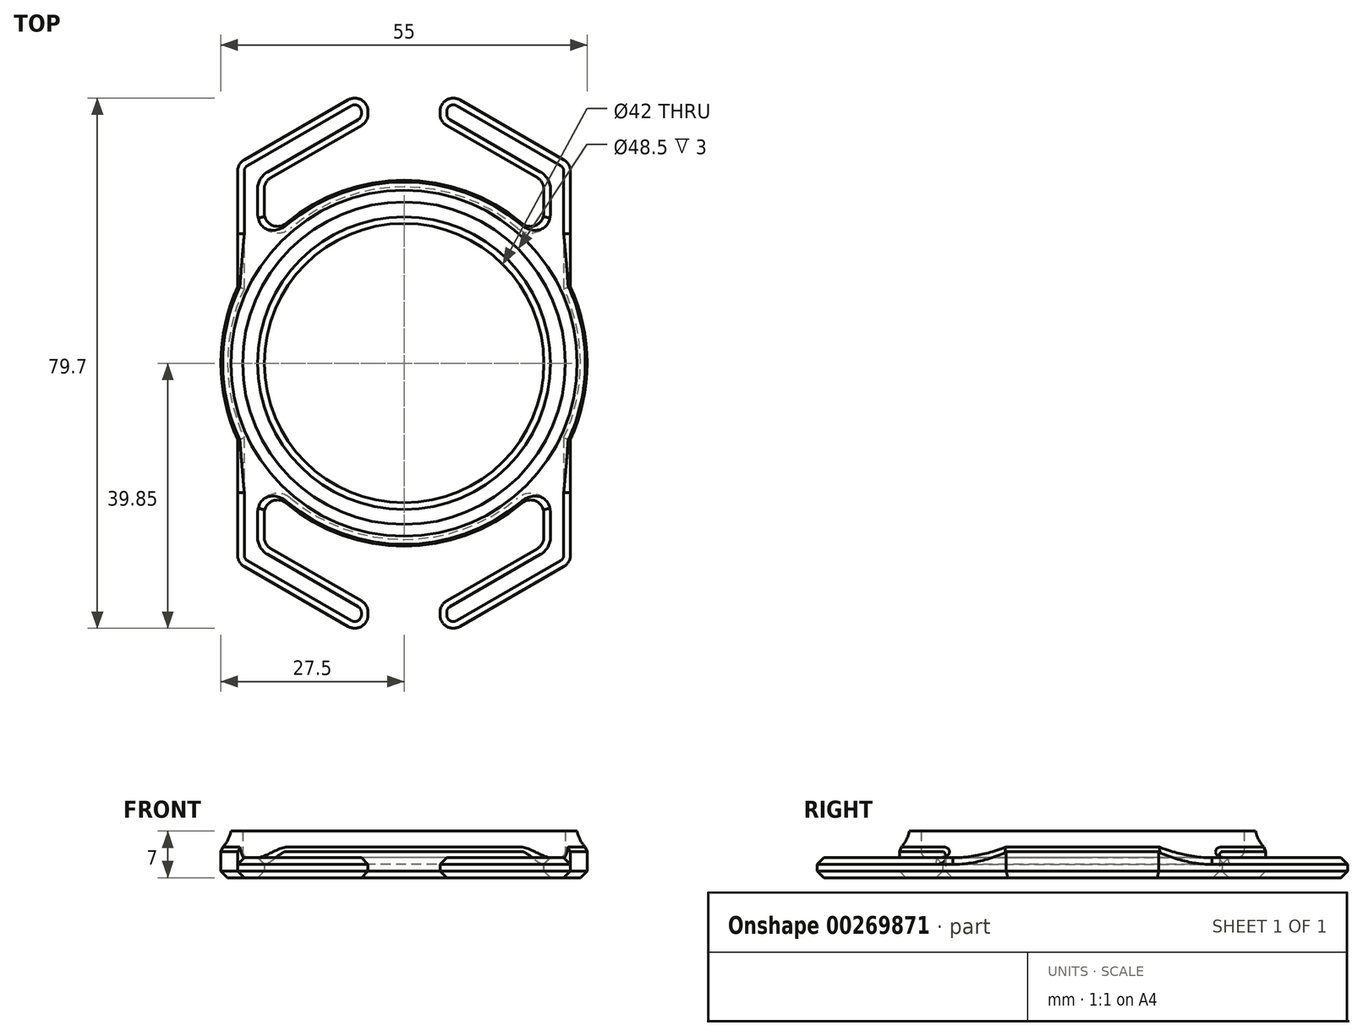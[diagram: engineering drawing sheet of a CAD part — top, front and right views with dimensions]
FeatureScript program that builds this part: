
annotation { "Feature Type Name" : "Feature", "Feature Type Description" : "" }
export const myFeature = defineFeature(function(context is Context, id is Id, definition is map)
    precondition{}
    {
        {
            var Q0;
            Q0=qCreatedBy(makeId("Top.planeOp"),FACE);
            var sketch = newSketch(context, id + "F0", { "sketchPlane" : qUnion([Q0])});
            skCircle(sketch, "E0", {"center": v(0, 0) * mm, "radius": 25 * mm});
            skLineSegment(sketch, "E1", {"start": v(-21, 27.3) * mm, "end": v(-5.41, 36.3) * mm});
            skLineSegment(sketch, "E2", {"start": v(-5.41, 36.3) * mm, "end": v(-5.41, 41.3) * mm});
            skLineSegment(sketch, "E3", {"start": v(-5.41, 41.3) * mm, "end": v(-25, 30) * mm});
            skLineSegment(sketch, "E4", {"start": v(-25, 30) * mm, "end": v(-25, 0) * mm});
            skLineSegment(sketch, "E5", {"start": v(-21, 27.3) * mm, "end": v(-21, 0) * mm});
            skCircle(sketch, "E6", {"center": v(0, 0) * mm, "radius": 21 * mm});
            skLineSegment(sketch, "E7", {"start": v(0, 0) * mm, "end": v(-21, 0) * mm, "construction": true});
            skLineSegment(sketch, "E8", {"start": v(-25, 0) * mm, "end": v(-21, 0) * mm});
            skLineSegment(sketch, "E9", {"start": v(0, 0) * mm, "end": v(0, 21) * mm, "construction": true});
            skLineSegment(sketch, "E10.MirrorCS", {"start": v(21, 27.3) * mm, "end": v(21, 0) * mm});
            skLineSegment(sketch, "E11.MirrorCS", {"start": v(25, 30) * mm, "end": v(25, 0) * mm});
            skLineSegment(sketch, "E12.MirrorCS", {"start": v(5.41, 41.3) * mm, "end": v(25, 30) * mm});
            skLineSegment(sketch, "E13.MirrorCS", {"start": v(21, 27.3) * mm, "end": v(5.41, 36.3) * mm});
            skLineSegment(sketch, "E14.MirrorCS", {"start": v(5.41, 36.3) * mm, "end": v(5.41, 41.3) * mm});
            skLineSegment(sketch, "E15.MirrorCS", {"start": v(-21, -27.3) * mm, "end": v(-21, 0) * mm});
            skLineSegment(sketch, "E16.MirrorCS", {"start": v(-25, -30) * mm, "end": v(-25, 0) * mm});
            skLineSegment(sketch, "E17.MirrorCS", {"start": v(-5.41, -41.3) * mm, "end": v(-25, -30) * mm});
            skLineSegment(sketch, "E18.MirrorCS", {"start": v(-21, -27.3) * mm, "end": v(-5.41, -36.3) * mm});
            skLineSegment(sketch, "E19.MirrorCS", {"start": v(-5.41, -36.3) * mm, "end": v(-5.41, -41.3) * mm});
            skLineSegment(sketch, "E20.MirrorCS", {"start": v(21, -27.3) * mm, "end": v(21, 0) * mm});
            skLineSegment(sketch, "E21.MirrorCS", {"start": v(25, -30) * mm, "end": v(25, 0) * mm});
            skLineSegment(sketch, "E22.MirrorCS", {"start": v(5.41, -41.3) * mm, "end": v(25, -30) * mm});
            skLineSegment(sketch, "E23.MirrorCS", {"start": v(21, -27.3) * mm, "end": v(5.41, -36.3) * mm});
            skLineSegment(sketch, "E24.MirrorCS", {"start": v(5.41, -36.3) * mm, "end": v(5.41, -41.3) * mm});
            skSolve(sketch);
        }
        {
            var Q0;
            Q0 = qSketchRegion(id + "F0", true);
            extrude(context, id + "F1", {"entities" : qUnion([Q0]), "depth" : 3 * mm});
        }
        {
            var Q0;
            Q0=makeQuery(id+"F1.opExtrude","CAP_FACE",FACE,{"disambiguationData":[OSD([sQuery(id+"F0.wireOp",EDGE,"E0"),sQuery(id+"F0.wireOp",EDGE,"E6")])],"isStart":false});
            var sketch = newSketch(context, id + "F2", { "sketchPlane" : qUnion([Q0])});
            skCircle(sketch, "E25", {"center": v(0, 0) * mm, "radius": 26 * mm});
            skCircle(sketch, "E26", {"center": v(0, 0) * mm, "radius": 24.25 * mm});
            skSolve(sketch);
        }
        {
            var Q0;
            Q0 = qSketchRegion(id + "F2", true);
            extrude(context, id + "F3", {"entities" : qUnion([Q0]), "operationType" : NewBodyOperationType.ADD, "depth" : 4 * mm});
        }
        {
            var Q0;
            Q0=qCreatedBy(makeId("Top.planeOp"),FACE);
            var sketch = newSketch(context, id + "F4", { "sketchPlane" : qUnion([Q0])});
            skCircle(sketch, "E27", {"center": v(0, 0) * mm, "radius": 27.5 * mm});
            skCircle(sketch, "E28", {"center": v(0, 0) * mm, "radius": 23 * mm});
            skSolve(sketch);
        }
        {
            var Q0;
            Q0 = qSketchRegion(id + "F4", true);
            extrude(context, id + "F5", {"entities" : qUnion([Q0]), "operationType" : NewBodyOperationType.ADD, "depth" : 3 * mm});
        }
        {
            var Q0;
            Q0=makeQuery(id+"F5.boolean.opBoolean","INTERSECT",EDGE,{"derivedFrom":[makeQuery(id+"F1.opExtrude","SWEPT_FACE",FACE,{"disambiguationData":[OSD([sQuery(id+"F0.wireOp",EDGE,"E5")])]}),makeQuery(id+"F5.opExtrude","SWEPT_FACE",FACE,{"disambiguationData":[OSD([sQuery(id+"F4.wireOp",EDGE,"E27")])]})]});
            var Q1;
            Q1=makeQuery(id+"F1.opExtrude","SWEPT_EDGE",EDGE,{"disambiguationData":[OSD([sQuery(id+"F0.wireOp",EDGE,"E1"),sQuery(id+"F0.wireOp",EDGE,"E5")])]});
            var Q2;
            Q2=makeQuery(id+"F1.opExtrude","SWEPT_EDGE",EDGE,{"disambiguationData":[OSD([sQuery(id+"F0.wireOp",EDGE,"E1"),sQuery(id+"F0.wireOp",EDGE,"E2")])]});
            var Q3;
            Q3=makeQuery(id+"F1.opExtrude","SWEPT_EDGE",EDGE,{"disambiguationData":[OSD([sQuery(id+"F0.wireOp",EDGE,"E2"),sQuery(id+"F0.wireOp",EDGE,"E3")])]});
            var Q4;
            Q4=makeQuery(id+"F1.opExtrude","SWEPT_EDGE",EDGE,{"disambiguationData":[OSD([sQuery(id+"F0.wireOp",EDGE,"E13.MirrorCS"),sQuery(id+"F0.wireOp",EDGE,"E14.MirrorCS")])]});
            var Q5;
            Q5=makeQuery(id+"F1.opExtrude","SWEPT_EDGE",EDGE,{"disambiguationData":[OSD([sQuery(id+"F0.wireOp",EDGE,"E12.MirrorCS"),sQuery(id+"F0.wireOp",EDGE,"E14.MirrorCS")])]});
            var Q6;
            Q6=makeQuery(id+"F1.opExtrude","SWEPT_EDGE",EDGE,{"disambiguationData":[OSD([sQuery(id+"F0.wireOp",EDGE,"E10.MirrorCS"),sQuery(id+"F0.wireOp",EDGE,"E13.MirrorCS")])]});
            var Q7;
            Q7=makeQuery(id+"F5.boolean.opBoolean","INTERSECT",EDGE,{"derivedFrom":[makeQuery(id+"F1.opExtrude","SWEPT_FACE",FACE,{"disambiguationData":[OSD([sQuery(id+"F0.wireOp",EDGE,"E10.MirrorCS")])]}),makeQuery(id+"F5.opExtrude","SWEPT_FACE",FACE,{"disambiguationData":[OSD([sQuery(id+"F4.wireOp",EDGE,"E27")])]})]});
            var Q8;
            Q8=makeQuery(id+"F1.opExtrude","SWEPT_EDGE",EDGE,{"disambiguationData":[OSD([sQuery(id+"F0.wireOp",EDGE,"E11.MirrorCS"),sQuery(id+"F0.wireOp",EDGE,"E12.MirrorCS")])]});
            var Q9;
            Q9=makeQuery(id+"F1.opExtrude","SWEPT_EDGE",EDGE,{"disambiguationData":[OSD([sQuery(id+"F0.wireOp",EDGE,"E3"),sQuery(id+"F0.wireOp",EDGE,"E4")])]});
            var Q10;
            Q10=makeQuery(id+"F5.boolean.opBoolean","INTERSECT",EDGE,{"derivedFrom":[makeQuery(id+"F1.opExtrude","SWEPT_FACE",FACE,{"disambiguationData":[OSD([sQuery(id+"F0.wireOp",EDGE,"E15.MirrorCS")])]}),makeQuery(id+"F5.opExtrude","SWEPT_FACE",FACE,{"disambiguationData":[OSD([sQuery(id+"F4.wireOp",EDGE,"E27")])]})]});
            var Q11;
            Q11=makeQuery(id+"F5.boolean.opBoolean","INTERSECT",EDGE,{"derivedFrom":[makeQuery(id+"F1.opExtrude","SWEPT_FACE",FACE,{"disambiguationData":[OSD([sQuery(id+"F0.wireOp",EDGE,"E20.MirrorCS")])]}),makeQuery(id+"F5.opExtrude","SWEPT_FACE",FACE,{"disambiguationData":[OSD([sQuery(id+"F4.wireOp",EDGE,"E27")])]})]});
            var Q12;
            Q12=makeQuery(id+"F1.opExtrude","SWEPT_EDGE",EDGE,{"disambiguationData":[OSD([sQuery(id+"F0.wireOp",EDGE,"E20.MirrorCS"),sQuery(id+"F0.wireOp",EDGE,"E23.MirrorCS")])]});
            var Q13;
            Q13=makeQuery(id+"F1.opExtrude","SWEPT_EDGE",EDGE,{"disambiguationData":[OSD([sQuery(id+"F0.wireOp",EDGE,"E23.MirrorCS"),sQuery(id+"F0.wireOp",EDGE,"E24.MirrorCS")])]});
            var Q14;
            Q14=makeQuery(id+"F1.opExtrude","SWEPT_EDGE",EDGE,{"disambiguationData":[OSD([sQuery(id+"F0.wireOp",EDGE,"E22.MirrorCS"),sQuery(id+"F0.wireOp",EDGE,"E24.MirrorCS")])]});
            var Q15;
            Q15=makeQuery(id+"F1.opExtrude","SWEPT_EDGE",EDGE,{"disambiguationData":[OSD([sQuery(id+"F0.wireOp",EDGE,"E15.MirrorCS"),sQuery(id+"F0.wireOp",EDGE,"E18.MirrorCS")])]});
            var Q16;
            Q16=makeQuery(id+"F1.opExtrude","SWEPT_EDGE",EDGE,{"disambiguationData":[OSD([sQuery(id+"F0.wireOp",EDGE,"E18.MirrorCS"),sQuery(id+"F0.wireOp",EDGE,"E19.MirrorCS")])]});
            var Q17;
            Q17=makeQuery(id+"F1.opExtrude","SWEPT_EDGE",EDGE,{"disambiguationData":[OSD([sQuery(id+"F0.wireOp",EDGE,"E17.MirrorCS"),sQuery(id+"F0.wireOp",EDGE,"E19.MirrorCS")])]});
            var Q18;
            Q18=makeQuery(id+"F1.opExtrude","SWEPT_EDGE",EDGE,{"disambiguationData":[OSD([sQuery(id+"F0.wireOp",EDGE,"E21.MirrorCS"),sQuery(id+"F0.wireOp",EDGE,"E22.MirrorCS")])]});
            var Q19;
            Q19=makeQuery(id+"F1.opExtrude","SWEPT_EDGE",EDGE,{"disambiguationData":[OSD([sQuery(id+"F0.wireOp",EDGE,"E16.MirrorCS"),sQuery(id+"F0.wireOp",EDGE,"E17.MirrorCS")])]});
            fillet(context, id + "F6", {"entities" : qUnion([Q0, Q1, Q2, Q3, Q4, Q5, Q6, Q7, Q8, Q9, Q10, Q11, Q12, Q13, Q14, Q15, Q16, Q17, Q18, Q19]), "radius" : 2 * mm, "tangentPropagation" : true, "allowEdgeOverflow" : false});
        }
        {
            var Q0;
            Q0=makeQuery(id+"F3.opExtrude","CAP_EDGE",EDGE,{"disambiguationData":[OSD([sQuery(id+"F2.wireOp",EDGE,"E26")])],"isStart":true});
            fillet(context, id + "F7", {"entities" : qUnion([Q0]), "radius" : 1 * mm, "tangentPropagation" : true, "allowEdgeOverflow" : false});
        }
        {
            var Q0;
            {var subQ0=sQuery(id+"F0.wireOp",EDGE,"E21.MirrorCS");var subQ1=sQuery(id+"F0.wireOp",EDGE,"E20.MirrorCS");var subQ2=sQuery(id+"F0.wireOp",EDGE,"E16.MirrorCS");var subQ3=sQuery(id+"F0.wireOp",EDGE,"E15.MirrorCS");var subQ4=sQuery(id+"F0.wireOp",EDGE,"E11.MirrorCS");var subQ5=sQuery(id+"F0.wireOp",EDGE,"E10.MirrorCS");var subQ6=sQuery(id+"F0.wireOp",EDGE,"E5");var subQ7=sQuery(id+"F0.wireOp",EDGE,"E4");var subQ8=makeQuery(id+"F1.opExtrude","CAP_FACE",FACE,{"disambiguationData":[OSD([sQuery(id+"F0.wireOp",EDGE,"E0"),sQuery(id+"F0.wireOp",EDGE,"E1"),sQuery(id+"F0.wireOp",EDGE,"E2"),sQuery(id+"F0.wireOp",EDGE,"E3"),subQ7,subQ6,sQuery(id+"F0.wireOp",EDGE,"E6"),subQ5,subQ4,sQuery(id+"F0.wireOp",EDGE,"E12.MirrorCS"),sQuery(id+"F0.wireOp",EDGE,"E13.MirrorCS"),sQuery(id+"F0.wireOp",EDGE,"E14.MirrorCS"),subQ3,subQ2,sQuery(id+"F0.wireOp",EDGE,"E17.MirrorCS"),sQuery(id+"F0.wireOp",EDGE,"E18.MirrorCS"),sQuery(id+"F0.wireOp",EDGE,"E19.MirrorCS"),subQ1,subQ0,sQuery(id+"F0.wireOp",EDGE,"E22.MirrorCS"),sQuery(id+"F0.wireOp",EDGE,"E23.MirrorCS"),sQuery(id+"F0.wireOp",EDGE,"E24.MirrorCS")])],"isStart":false});var subQ9=makeQuery(id+"F1.opExtrude","SWEPT_FACE",FACE,{"disambiguationData":[OSD([subQ4,subQ0])]});var subQ10=sQuery(id+"F2.wireOp",EDGE,"E25");var subQ11=makeQuery(id+"F3.opExtrude","SWEPT_FACE",FACE,{"disambiguationData":[OSD([subQ10])]});var subQ12=makeQuery(id+"F3.opExtrude","CAP_FACE",FACE,{"disambiguationData":[OSD([subQ10,sQuery(id+"F2.wireOp",EDGE,"E26")])],"isStart":true});var subQ13=makeQuery(id+"F3.opExtrude","CAP_EDGE",EDGE,{"disambiguationData":[OSD([subQ10])],"isStart":true});var subQ14=makeQuery(id+"F1.opExtrude","SWEPT_FACE",FACE,{"disambiguationData":[OSD([subQ7,subQ2])]});var subQ15=makeQuery(id+"F1.opExtrude","SWEPT_FACE",FACE,{"disambiguationData":[OSD([subQ1])]});var subQ16=makeQuery(id+"F1.opExtrude","SWEPT_FACE",FACE,{"disambiguationData":[OSD([subQ3])]});var subQ17=makeQuery(id+"F1.opExtrude","SWEPT_FACE",FACE,{"disambiguationData":[OSD([subQ5])]});var subQ18=makeQuery(id+"F1.opExtrude","SWEPT_FACE",FACE,{"disambiguationData":[OSD([subQ6])]});Q0=makeQuery(id+"F5.boolean.opBoolean","MERGE",EDGE,{"derivedFrom":[makeQuery(id+"F3.boolean.opBoolean","SPLIT",EDGE,{"disambiguationData":[topologyDisambiguationEdgeConnected([subQ11,subQ12]),TD([subQ18])],"derivedFrom":subQ13}),makeQuery(id+"F3.boolean.opBoolean","SPLIT",EDGE,{"disambiguationData":[topologyDisambiguationEdgeConnected([subQ11,subQ12]),TD([subQ16])],"derivedFrom":subQ13}),makeQuery(id+"F3.boolean.opBoolean","SPLIT",EDGE,{"disambiguationData":[topologyDisambiguationEdgeConnected([subQ8,subQ11]),TD([subQ18])],"derivedFrom":subQ13}),makeQuery(id+"F3.boolean.opBoolean","SPLIT",EDGE,{"disambiguationData":[topologyDisambiguationEdgeConnected([subQ8,subQ11]),TD([subQ17])],"derivedFrom":subQ13}),makeQuery(id+"F3.boolean.opBoolean","SPLIT",EDGE,{"disambiguationData":[topologyDisambiguationEdgeConnected([subQ8,subQ11]),TD([subQ16])],"derivedFrom":subQ13}),makeQuery(id+"F3.boolean.opBoolean","SPLIT",EDGE,{"disambiguationData":[topologyDisambiguationEdgeConnected([subQ8,subQ11]),TD([subQ15])],"derivedFrom":subQ13}),makeQuery(id+"F3.boolean.opBoolean","SPLIT",EDGE,{"disambiguationData":[topologyDisambiguationEdgeConnected([subQ11,subQ12]),TD([subQ14])],"derivedFrom":subQ13}),makeQuery(id+"F3.boolean.opBoolean","SPLIT",EDGE,{"disambiguationData":[topologyDisambiguationEdgeConnected([subQ11,subQ12]),TD([subQ9])],"derivedFrom":subQ13})]});}
            fillet(context, id + "F8", {"entities" : qUnion([Q0]), "radius" : 5 * mm, "tangentPropagation" : true, "allowEdgeOverflow" : false});
        }
        {
            var Q0;
            {var subQ0=sQuery(id+"F4.wireOp",EDGE,"E27");var subQ2=sQuery(id+"F0.wireOp",EDGE,"E15.MirrorCS");Q0=makeQuery(id+"F5.boolean.opBoolean","SPLIT",EDGE,{"disambiguationData":[TD([makeQuery(id+"F1.opExtrude","SWEPT_FACE",FACE,{"disambiguationData":[OSD([subQ2])]})])],"derivedFrom":makeQuery(id+"F5.opExtrude","CAP_EDGE",EDGE,{"disambiguationData":[OSD([subQ0])],"isStart":true})});}
            var Q1;
            {var subQ0=sQuery(id+"F0.wireOp",EDGE,"E20.MirrorCS");var subQ1=makeQuery(id+"F1.opExtrude","SWEPT_FACE",FACE,{"disambiguationData":[OSD([subQ0])]});var subQ3=sQuery(id+"F4.wireOp",EDGE,"E27");var subQ4=sQuery(id+"F0.wireOp",EDGE,"E15.MirrorCS");var subQ5=makeQuery(id+"F1.opExtrude","SWEPT_FACE",FACE,{"disambiguationData":[OSD([subQ4])]});var subQ6=sQuery(id+"F0.wireOp",EDGE,"E24.MirrorCS");var subQ7=sQuery(id+"F0.wireOp",EDGE,"E23.MirrorCS");var subQ8=sQuery(id+"F0.wireOp",EDGE,"E22.MirrorCS");var subQ9=sQuery(id+"F0.wireOp",EDGE,"E21.MirrorCS");var subQ10=sQuery(id+"F0.wireOp",EDGE,"E19.MirrorCS");var subQ11=sQuery(id+"F0.wireOp",EDGE,"E18.MirrorCS");var subQ12=sQuery(id+"F0.wireOp",EDGE,"E17.MirrorCS");var subQ13=sQuery(id+"F0.wireOp",EDGE,"E16.MirrorCS");var subQ14=sQuery(id+"F0.wireOp",EDGE,"E14.MirrorCS");var subQ15=sQuery(id+"F0.wireOp",EDGE,"E13.MirrorCS");var subQ16=sQuery(id+"F0.wireOp",EDGE,"E12.MirrorCS");var subQ17=sQuery(id+"F0.wireOp",EDGE,"E11.MirrorCS");var subQ18=sQuery(id+"F0.wireOp",EDGE,"E10.MirrorCS");var subQ19=sQuery(id+"F0.wireOp",EDGE,"E6");var subQ20=sQuery(id+"F0.wireOp",EDGE,"E5");var subQ21=sQuery(id+"F0.wireOp",EDGE,"E4");var subQ22=sQuery(id+"F0.wireOp",EDGE,"E3");var subQ23=sQuery(id+"F0.wireOp",EDGE,"E2");var subQ24=sQuery(id+"F0.wireOp",EDGE,"E1");var subQ25=sQuery(id+"F0.wireOp",EDGE,"E0");var subQ26=makeQuery(id+"F1.opExtrude","CAP_FACE",FACE,{"disambiguationData":[OSD([subQ25,subQ24,subQ23,subQ22,subQ21,subQ20,subQ19,subQ18,subQ17,subQ16,subQ15,subQ14,subQ4,subQ13,subQ12,subQ11,subQ10,subQ0,subQ9,subQ8,subQ7,subQ6])],"isStart":false});var subQ27=makeQuery(id+"F1.opExtrude","SWEPT_FACE",FACE,{"disambiguationData":[OSD([subQ17,subQ9])]});var subQ28=sQuery(id+"F2.wireOp",EDGE,"E25");var subQ29=makeQuery(id+"F3.opExtrude","SWEPT_FACE",FACE,{"disambiguationData":[OSD([subQ28])]});var subQ30=makeQuery(id+"F3.opExtrude","CAP_FACE",FACE,{"disambiguationData":[OSD([subQ28,sQuery(id+"F2.wireOp",EDGE,"E26")])],"isStart":true});var subQ31=makeQuery(id+"F3.opExtrude","CAP_EDGE",EDGE,{"disambiguationData":[OSD([subQ28])],"isStart":true});var subQ32=makeQuery(id+"F1.opExtrude","SWEPT_FACE",FACE,{"disambiguationData":[OSD([subQ21,subQ13])]});var subQ33=makeQuery(id+"F1.opExtrude","SWEPT_FACE",FACE,{"disambiguationData":[OSD([subQ18])]});var subQ34=makeQuery(id+"F1.opExtrude","SWEPT_FACE",FACE,{"disambiguationData":[OSD([subQ20])]});Q1=makeQuery(id+"F8.opFillet","BLEND_EDGE",EDGE,{"blendedFrom":[makeQuery(id+"F5.boolean.opBoolean","MERGE",EDGE,{"derivedFrom":[makeQuery(id+"F3.boolean.opBoolean","SPLIT",EDGE,{"disambiguationData":[topologyDisambiguationEdgeConnected([subQ29,subQ30]),TD([subQ34])],"derivedFrom":subQ31}),makeQuery(id+"F3.boolean.opBoolean","SPLIT",EDGE,{"disambiguationData":[topologyDisambiguationEdgeConnected([subQ29,subQ30]),TD([subQ5])],"derivedFrom":subQ31}),makeQuery(id+"F3.boolean.opBoolean","SPLIT",EDGE,{"disambiguationData":[topologyDisambiguationEdgeConnected([subQ26,subQ29]),TD([subQ34])],"derivedFrom":subQ31}),makeQuery(id+"F3.boolean.opBoolean","SPLIT",EDGE,{"disambiguationData":[topologyDisambiguationEdgeConnected([subQ26,subQ29]),TD([subQ33])],"derivedFrom":subQ31}),makeQuery(id+"F3.boolean.opBoolean","SPLIT",EDGE,{"disambiguationData":[topologyDisambiguationEdgeConnected([subQ26,subQ29]),TD([subQ5])],"derivedFrom":subQ31}),makeQuery(id+"F3.boolean.opBoolean","SPLIT",EDGE,{"disambiguationData":[topologyDisambiguationEdgeConnected([subQ26,subQ29]),TD([subQ1])],"derivedFrom":subQ31}),makeQuery(id+"F3.boolean.opBoolean","SPLIT",EDGE,{"disambiguationData":[topologyDisambiguationEdgeConnected([subQ29,subQ30]),TD([subQ32])],"derivedFrom":subQ31}),makeQuery(id+"F3.boolean.opBoolean","SPLIT",EDGE,{"disambiguationData":[topologyDisambiguationEdgeConnected([subQ29,subQ30]),TD([subQ27])],"derivedFrom":subQ31})]}),makeQuery(id+"F5.boolean.opBoolean","SPLIT",FACE,{"disambiguationData":[TD([subQ5])],"derivedFrom":makeQuery(id+"F5.opExtrude","SWEPT_FACE",FACE,{"disambiguationData":[OSD([subQ3])]})})],"blendedInto":[makeQuery(id+"F5.boolean.opBoolean","SPLIT",FACE,{"disambiguationData":[TD([subQ5])],"derivedFrom":makeQuery(id+"F5.opExtrude","SWEPT_FACE",FACE,{"disambiguationData":[OSD([subQ3])]})})]});}
            var Q2;
            {var subQ0=sQuery(id+"F4.wireOp",EDGE,"E27");var subQ2=sQuery(id+"F0.wireOp",EDGE,"E5");Q2=makeQuery(id+"F5.boolean.opBoolean","SPLIT",EDGE,{"disambiguationData":[TD([makeQuery(id+"F1.opExtrude","SWEPT_FACE",FACE,{"disambiguationData":[OSD([subQ2])]})])],"derivedFrom":makeQuery(id+"F5.opExtrude","CAP_EDGE",EDGE,{"disambiguationData":[OSD([subQ0])],"isStart":true})});}
            var Q3;
            {var subQ0=sQuery(id+"F0.wireOp",EDGE,"E10.MirrorCS");var subQ1=makeQuery(id+"F1.opExtrude","SWEPT_FACE",FACE,{"disambiguationData":[OSD([subQ0])]});var subQ2=sQuery(id+"F0.wireOp",EDGE,"E5");var subQ3=makeQuery(id+"F1.opExtrude","SWEPT_FACE",FACE,{"disambiguationData":[OSD([subQ2])]});var subQ5=sQuery(id+"F4.wireOp",EDGE,"E27");var subQ6=sQuery(id+"F0.wireOp",EDGE,"E24.MirrorCS");var subQ7=sQuery(id+"F0.wireOp",EDGE,"E23.MirrorCS");var subQ8=sQuery(id+"F0.wireOp",EDGE,"E22.MirrorCS");var subQ9=sQuery(id+"F0.wireOp",EDGE,"E21.MirrorCS");var subQ10=sQuery(id+"F0.wireOp",EDGE,"E20.MirrorCS");var subQ11=sQuery(id+"F0.wireOp",EDGE,"E19.MirrorCS");var subQ12=sQuery(id+"F0.wireOp",EDGE,"E18.MirrorCS");var subQ13=sQuery(id+"F0.wireOp",EDGE,"E17.MirrorCS");var subQ14=sQuery(id+"F0.wireOp",EDGE,"E16.MirrorCS");var subQ15=sQuery(id+"F0.wireOp",EDGE,"E15.MirrorCS");var subQ16=sQuery(id+"F0.wireOp",EDGE,"E14.MirrorCS");var subQ17=sQuery(id+"F0.wireOp",EDGE,"E13.MirrorCS");var subQ18=sQuery(id+"F0.wireOp",EDGE,"E12.MirrorCS");var subQ19=sQuery(id+"F0.wireOp",EDGE,"E11.MirrorCS");var subQ20=sQuery(id+"F0.wireOp",EDGE,"E6");var subQ21=sQuery(id+"F0.wireOp",EDGE,"E4");var subQ22=sQuery(id+"F0.wireOp",EDGE,"E3");var subQ23=sQuery(id+"F0.wireOp",EDGE,"E2");var subQ24=sQuery(id+"F0.wireOp",EDGE,"E1");var subQ25=sQuery(id+"F0.wireOp",EDGE,"E0");var subQ26=makeQuery(id+"F1.opExtrude","CAP_FACE",FACE,{"disambiguationData":[OSD([subQ25,subQ24,subQ23,subQ22,subQ21,subQ2,subQ20,subQ0,subQ19,subQ18,subQ17,subQ16,subQ15,subQ14,subQ13,subQ12,subQ11,subQ10,subQ9,subQ8,subQ7,subQ6])],"isStart":false});var subQ27=makeQuery(id+"F1.opExtrude","SWEPT_FACE",FACE,{"disambiguationData":[OSD([subQ19,subQ9])]});var subQ28=sQuery(id+"F2.wireOp",EDGE,"E25");var subQ29=makeQuery(id+"F3.opExtrude","SWEPT_FACE",FACE,{"disambiguationData":[OSD([subQ28])]});var subQ30=makeQuery(id+"F3.opExtrude","CAP_FACE",FACE,{"disambiguationData":[OSD([subQ28,sQuery(id+"F2.wireOp",EDGE,"E26")])],"isStart":true});var subQ31=makeQuery(id+"F3.opExtrude","CAP_EDGE",EDGE,{"disambiguationData":[OSD([subQ28])],"isStart":true});var subQ32=makeQuery(id+"F1.opExtrude","SWEPT_FACE",FACE,{"disambiguationData":[OSD([subQ21,subQ14])]});var subQ33=makeQuery(id+"F1.opExtrude","SWEPT_FACE",FACE,{"disambiguationData":[OSD([subQ10])]});var subQ34=makeQuery(id+"F1.opExtrude","SWEPT_FACE",FACE,{"disambiguationData":[OSD([subQ15])]});Q3=makeQuery(id+"F8.opFillet","BLEND_EDGE",EDGE,{"blendedFrom":[makeQuery(id+"F5.boolean.opBoolean","MERGE",EDGE,{"derivedFrom":[makeQuery(id+"F3.boolean.opBoolean","SPLIT",EDGE,{"disambiguationData":[topologyDisambiguationEdgeConnected([subQ29,subQ30]),TD([subQ3])],"derivedFrom":subQ31}),makeQuery(id+"F3.boolean.opBoolean","SPLIT",EDGE,{"disambiguationData":[topologyDisambiguationEdgeConnected([subQ29,subQ30]),TD([subQ34])],"derivedFrom":subQ31}),makeQuery(id+"F3.boolean.opBoolean","SPLIT",EDGE,{"disambiguationData":[topologyDisambiguationEdgeConnected([subQ26,subQ29]),TD([subQ3])],"derivedFrom":subQ31}),makeQuery(id+"F3.boolean.opBoolean","SPLIT",EDGE,{"disambiguationData":[topologyDisambiguationEdgeConnected([subQ26,subQ29]),TD([subQ1])],"derivedFrom":subQ31}),makeQuery(id+"F3.boolean.opBoolean","SPLIT",EDGE,{"disambiguationData":[topologyDisambiguationEdgeConnected([subQ26,subQ29]),TD([subQ34])],"derivedFrom":subQ31}),makeQuery(id+"F3.boolean.opBoolean","SPLIT",EDGE,{"disambiguationData":[topologyDisambiguationEdgeConnected([subQ26,subQ29]),TD([subQ33])],"derivedFrom":subQ31}),makeQuery(id+"F3.boolean.opBoolean","SPLIT",EDGE,{"disambiguationData":[topologyDisambiguationEdgeConnected([subQ29,subQ30]),TD([subQ32])],"derivedFrom":subQ31}),makeQuery(id+"F3.boolean.opBoolean","SPLIT",EDGE,{"disambiguationData":[topologyDisambiguationEdgeConnected([subQ29,subQ30]),TD([subQ27])],"derivedFrom":subQ31})]}),makeQuery(id+"F5.boolean.opBoolean","SPLIT",FACE,{"disambiguationData":[TD([subQ3])],"derivedFrom":makeQuery(id+"F5.opExtrude","SWEPT_FACE",FACE,{"disambiguationData":[OSD([subQ5])]})})],"blendedInto":[makeQuery(id+"F5.boolean.opBoolean","SPLIT",FACE,{"disambiguationData":[TD([subQ3])],"derivedFrom":makeQuery(id+"F5.opExtrude","SWEPT_FACE",FACE,{"disambiguationData":[OSD([subQ5])]})})]});}
            var Q4;
            {var subQ1=sQuery(id+"F4.wireOp",EDGE,"E27");var subQ2=sQuery(id+"F0.wireOp",EDGE,"E24.MirrorCS");var subQ3=sQuery(id+"F0.wireOp",EDGE,"E23.MirrorCS");var subQ4=sQuery(id+"F0.wireOp",EDGE,"E22.MirrorCS");var subQ5=sQuery(id+"F0.wireOp",EDGE,"E21.MirrorCS");var subQ6=sQuery(id+"F0.wireOp",EDGE,"E20.MirrorCS");var subQ7=sQuery(id+"F0.wireOp",EDGE,"E19.MirrorCS");var subQ8=sQuery(id+"F0.wireOp",EDGE,"E18.MirrorCS");var subQ9=sQuery(id+"F0.wireOp",EDGE,"E17.MirrorCS");var subQ10=sQuery(id+"F0.wireOp",EDGE,"E16.MirrorCS");var subQ11=sQuery(id+"F0.wireOp",EDGE,"E15.MirrorCS");var subQ12=sQuery(id+"F0.wireOp",EDGE,"E14.MirrorCS");var subQ13=sQuery(id+"F0.wireOp",EDGE,"E13.MirrorCS");var subQ14=sQuery(id+"F0.wireOp",EDGE,"E12.MirrorCS");var subQ15=sQuery(id+"F0.wireOp",EDGE,"E11.MirrorCS");var subQ16=sQuery(id+"F0.wireOp",EDGE,"E10.MirrorCS");var subQ17=sQuery(id+"F0.wireOp",EDGE,"E6");var subQ18=sQuery(id+"F0.wireOp",EDGE,"E5");var subQ19=sQuery(id+"F0.wireOp",EDGE,"E4");var subQ20=sQuery(id+"F0.wireOp",EDGE,"E3");var subQ21=sQuery(id+"F0.wireOp",EDGE,"E2");var subQ22=sQuery(id+"F0.wireOp",EDGE,"E1");var subQ23=sQuery(id+"F0.wireOp",EDGE,"E0");var subQ24=makeQuery(id+"F1.opExtrude","CAP_FACE",FACE,{"disambiguationData":[OSD([subQ23,subQ22,subQ21,subQ20,subQ19,subQ18,subQ17,subQ16,subQ15,subQ14,subQ13,subQ12,subQ11,subQ10,subQ9,subQ8,subQ7,subQ6,subQ5,subQ4,subQ3,subQ2])],"isStart":false});var subQ25=makeQuery(id+"F1.opExtrude","SWEPT_FACE",FACE,{"disambiguationData":[OSD([subQ15,subQ5])]});var subQ26=sQuery(id+"F2.wireOp",EDGE,"E25");var subQ27=makeQuery(id+"F3.opExtrude","SWEPT_FACE",FACE,{"disambiguationData":[OSD([subQ26])]});var subQ28=makeQuery(id+"F3.opExtrude","CAP_FACE",FACE,{"disambiguationData":[OSD([subQ26,sQuery(id+"F2.wireOp",EDGE,"E26")])],"isStart":true});var subQ29=makeQuery(id+"F3.opExtrude","CAP_EDGE",EDGE,{"disambiguationData":[OSD([subQ26])],"isStart":true});var subQ30=makeQuery(id+"F1.opExtrude","SWEPT_FACE",FACE,{"disambiguationData":[OSD([subQ19,subQ10])]});var subQ31=makeQuery(id+"F1.opExtrude","SWEPT_FACE",FACE,{"disambiguationData":[OSD([subQ6])]});var subQ32=makeQuery(id+"F1.opExtrude","SWEPT_FACE",FACE,{"disambiguationData":[OSD([subQ11])]});var subQ33=makeQuery(id+"F1.opExtrude","SWEPT_FACE",FACE,{"disambiguationData":[OSD([subQ16])]});var subQ34=makeQuery(id+"F1.opExtrude","SWEPT_FACE",FACE,{"disambiguationData":[OSD([subQ18])]});Q4=makeQuery(id+"F8.opFillet","BLEND_EDGE",EDGE,{"blendedFrom":[makeQuery(id+"F5.boolean.opBoolean","MERGE",EDGE,{"derivedFrom":[makeQuery(id+"F3.boolean.opBoolean","SPLIT",EDGE,{"disambiguationData":[topologyDisambiguationEdgeConnected([subQ27,subQ28]),TD([subQ34])],"derivedFrom":subQ29}),makeQuery(id+"F3.boolean.opBoolean","SPLIT",EDGE,{"disambiguationData":[topologyDisambiguationEdgeConnected([subQ27,subQ28]),TD([subQ32])],"derivedFrom":subQ29}),makeQuery(id+"F3.boolean.opBoolean","SPLIT",EDGE,{"disambiguationData":[topologyDisambiguationEdgeConnected([subQ24,subQ27]),TD([subQ34])],"derivedFrom":subQ29}),makeQuery(id+"F3.boolean.opBoolean","SPLIT",EDGE,{"disambiguationData":[topologyDisambiguationEdgeConnected([subQ24,subQ27]),TD([subQ33])],"derivedFrom":subQ29}),makeQuery(id+"F3.boolean.opBoolean","SPLIT",EDGE,{"disambiguationData":[topologyDisambiguationEdgeConnected([subQ24,subQ27]),TD([subQ32])],"derivedFrom":subQ29}),makeQuery(id+"F3.boolean.opBoolean","SPLIT",EDGE,{"disambiguationData":[topologyDisambiguationEdgeConnected([subQ24,subQ27]),TD([subQ31])],"derivedFrom":subQ29}),makeQuery(id+"F3.boolean.opBoolean","SPLIT",EDGE,{"disambiguationData":[topologyDisambiguationEdgeConnected([subQ27,subQ28]),TD([subQ30])],"derivedFrom":subQ29}),makeQuery(id+"F3.boolean.opBoolean","SPLIT",EDGE,{"disambiguationData":[topologyDisambiguationEdgeConnected([subQ27,subQ28]),TD([subQ25])],"derivedFrom":subQ29})]}),makeQuery(id+"F5.boolean.opBoolean","SPLIT",FACE,{"disambiguationData":[TD([subQ25])],"derivedFrom":makeQuery(id+"F5.opExtrude","SWEPT_FACE",FACE,{"disambiguationData":[OSD([subQ1])]})})],"blendedInto":[makeQuery(id+"F5.boolean.opBoolean","SPLIT",FACE,{"disambiguationData":[TD([subQ25])],"derivedFrom":makeQuery(id+"F5.opExtrude","SWEPT_FACE",FACE,{"disambiguationData":[OSD([subQ1])]})})]});}
            var Q5;
            {var subQ1=sQuery(id+"F0.wireOp",EDGE,"E12.MirrorCS");var subQ2=sQuery(id+"F0.wireOp",EDGE,"E24.MirrorCS");var subQ3=sQuery(id+"F0.wireOp",EDGE,"E23.MirrorCS");var subQ4=sQuery(id+"F0.wireOp",EDGE,"E22.MirrorCS");var subQ5=sQuery(id+"F0.wireOp",EDGE,"E21.MirrorCS");var subQ6=sQuery(id+"F0.wireOp",EDGE,"E20.MirrorCS");var subQ7=sQuery(id+"F0.wireOp",EDGE,"E19.MirrorCS");var subQ8=sQuery(id+"F0.wireOp",EDGE,"E18.MirrorCS");var subQ9=sQuery(id+"F0.wireOp",EDGE,"E17.MirrorCS");var subQ10=sQuery(id+"F0.wireOp",EDGE,"E16.MirrorCS");var subQ11=sQuery(id+"F0.wireOp",EDGE,"E15.MirrorCS");var subQ12=sQuery(id+"F0.wireOp",EDGE,"E14.MirrorCS");var subQ13=sQuery(id+"F0.wireOp",EDGE,"E13.MirrorCS");var subQ14=sQuery(id+"F0.wireOp",EDGE,"E11.MirrorCS");var subQ15=sQuery(id+"F0.wireOp",EDGE,"E10.MirrorCS");var subQ16=sQuery(id+"F0.wireOp",EDGE,"E6");var subQ17=sQuery(id+"F0.wireOp",EDGE,"E5");var subQ18=sQuery(id+"F0.wireOp",EDGE,"E4");var subQ19=sQuery(id+"F0.wireOp",EDGE,"E3");var subQ20=sQuery(id+"F0.wireOp",EDGE,"E2");var subQ21=sQuery(id+"F0.wireOp",EDGE,"E1");var subQ22=sQuery(id+"F0.wireOp",EDGE,"E0");var subQ23=makeQuery(id+"F1.opExtrude","CAP_FACE",FACE,{"disambiguationData":[OSD([subQ22,subQ21,subQ20,subQ19,subQ18,subQ17,subQ16,subQ15,subQ14,subQ1,subQ13,subQ12,subQ11,subQ10,subQ9,subQ8,subQ7,subQ6,subQ5,subQ4,subQ3,subQ2])],"isStart":false});var subQ25=makeQuery(id+"F1.opExtrude","SWEPT_FACE",FACE,{"disambiguationData":[OSD([subQ14,subQ5])]});var subQ26=sQuery(id+"F2.wireOp",EDGE,"E25");var subQ27=makeQuery(id+"F3.opExtrude","SWEPT_FACE",FACE,{"disambiguationData":[OSD([subQ26])]});var subQ28=makeQuery(id+"F3.opExtrude","CAP_FACE",FACE,{"disambiguationData":[OSD([subQ26,sQuery(id+"F2.wireOp",EDGE,"E26")])],"isStart":true});var subQ29=makeQuery(id+"F3.opExtrude","CAP_EDGE",EDGE,{"disambiguationData":[OSD([subQ26])],"isStart":true});var subQ30=makeQuery(id+"F1.opExtrude","SWEPT_FACE",FACE,{"disambiguationData":[OSD([subQ18,subQ10])]});var subQ31=makeQuery(id+"F1.opExtrude","SWEPT_FACE",FACE,{"disambiguationData":[OSD([subQ6])]});var subQ32=makeQuery(id+"F1.opExtrude","SWEPT_FACE",FACE,{"disambiguationData":[OSD([subQ11])]});var subQ33=makeQuery(id+"F1.opExtrude","SWEPT_FACE",FACE,{"disambiguationData":[OSD([subQ15])]});var subQ34=makeQuery(id+"F1.opExtrude","SWEPT_FACE",FACE,{"disambiguationData":[OSD([subQ17])]});Q5=makeQuery(id+"F8.opFillet","BLEND_EDGE",EDGE,{"blendedFrom":[makeQuery(id+"F5.boolean.opBoolean","MERGE",EDGE,{"derivedFrom":[makeQuery(id+"F3.boolean.opBoolean","SPLIT",EDGE,{"disambiguationData":[topologyDisambiguationEdgeConnected([subQ27,subQ28]),TD([subQ34])],"derivedFrom":subQ29}),makeQuery(id+"F3.boolean.opBoolean","SPLIT",EDGE,{"disambiguationData":[topologyDisambiguationEdgeConnected([subQ27,subQ28]),TD([subQ32])],"derivedFrom":subQ29}),makeQuery(id+"F3.boolean.opBoolean","SPLIT",EDGE,{"disambiguationData":[topologyDisambiguationEdgeConnected([subQ23,subQ27]),TD([subQ34])],"derivedFrom":subQ29}),makeQuery(id+"F3.boolean.opBoolean","SPLIT",EDGE,{"disambiguationData":[topologyDisambiguationEdgeConnected([subQ23,subQ27]),TD([subQ33])],"derivedFrom":subQ29}),makeQuery(id+"F3.boolean.opBoolean","SPLIT",EDGE,{"disambiguationData":[topologyDisambiguationEdgeConnected([subQ23,subQ27]),TD([subQ32])],"derivedFrom":subQ29}),makeQuery(id+"F3.boolean.opBoolean","SPLIT",EDGE,{"disambiguationData":[topologyDisambiguationEdgeConnected([subQ23,subQ27]),TD([subQ31])],"derivedFrom":subQ29}),makeQuery(id+"F3.boolean.opBoolean","SPLIT",EDGE,{"disambiguationData":[topologyDisambiguationEdgeConnected([subQ27,subQ28]),TD([subQ30])],"derivedFrom":subQ29}),makeQuery(id+"F3.boolean.opBoolean","SPLIT",EDGE,{"disambiguationData":[topologyDisambiguationEdgeConnected([subQ27,subQ28]),TD([subQ25])],"derivedFrom":subQ29})]}),makeQuery(id+"F5.boolean.opBoolean","SPLIT",FACE,{"disambiguationData":[TD([makeQuery(id+"F1.opExtrude","SWEPT_FACE",FACE,{"disambiguationData":[OSD([subQ1])]})])],"derivedFrom":subQ25})],"blendedInto":[makeQuery(id+"F5.boolean.opBoolean","SPLIT",FACE,{"disambiguationData":[TD([makeQuery(id+"F1.opExtrude","SWEPT_FACE",FACE,{"disambiguationData":[OSD([subQ1])]})])],"derivedFrom":subQ25})]});}
            var Q6;
            {var subQ0=sQuery(id+"F0.wireOp",EDGE,"E22.MirrorCS");var subQ2=sQuery(id+"F0.wireOp",EDGE,"E24.MirrorCS");var subQ3=sQuery(id+"F0.wireOp",EDGE,"E23.MirrorCS");var subQ4=sQuery(id+"F0.wireOp",EDGE,"E21.MirrorCS");var subQ5=sQuery(id+"F0.wireOp",EDGE,"E20.MirrorCS");var subQ6=sQuery(id+"F0.wireOp",EDGE,"E19.MirrorCS");var subQ7=sQuery(id+"F0.wireOp",EDGE,"E18.MirrorCS");var subQ8=sQuery(id+"F0.wireOp",EDGE,"E17.MirrorCS");var subQ9=sQuery(id+"F0.wireOp",EDGE,"E16.MirrorCS");var subQ10=sQuery(id+"F0.wireOp",EDGE,"E15.MirrorCS");var subQ11=sQuery(id+"F0.wireOp",EDGE,"E14.MirrorCS");var subQ12=sQuery(id+"F0.wireOp",EDGE,"E13.MirrorCS");var subQ13=sQuery(id+"F0.wireOp",EDGE,"E12.MirrorCS");var subQ14=sQuery(id+"F0.wireOp",EDGE,"E11.MirrorCS");var subQ15=sQuery(id+"F0.wireOp",EDGE,"E10.MirrorCS");var subQ16=sQuery(id+"F0.wireOp",EDGE,"E6");var subQ17=sQuery(id+"F0.wireOp",EDGE,"E5");var subQ18=sQuery(id+"F0.wireOp",EDGE,"E4");var subQ19=sQuery(id+"F0.wireOp",EDGE,"E3");var subQ20=sQuery(id+"F0.wireOp",EDGE,"E2");var subQ21=sQuery(id+"F0.wireOp",EDGE,"E1");var subQ22=sQuery(id+"F0.wireOp",EDGE,"E0");var subQ23=makeQuery(id+"F1.opExtrude","CAP_FACE",FACE,{"disambiguationData":[OSD([subQ22,subQ21,subQ20,subQ19,subQ18,subQ17,subQ16,subQ15,subQ14,subQ13,subQ12,subQ11,subQ10,subQ9,subQ8,subQ7,subQ6,subQ5,subQ4,subQ0,subQ3,subQ2])],"isStart":false});var subQ25=makeQuery(id+"F1.opExtrude","SWEPT_FACE",FACE,{"disambiguationData":[OSD([subQ14,subQ4])]});var subQ26=sQuery(id+"F2.wireOp",EDGE,"E25");var subQ27=makeQuery(id+"F3.opExtrude","SWEPT_FACE",FACE,{"disambiguationData":[OSD([subQ26])]});var subQ28=makeQuery(id+"F3.opExtrude","CAP_FACE",FACE,{"disambiguationData":[OSD([subQ26,sQuery(id+"F2.wireOp",EDGE,"E26")])],"isStart":true});var subQ29=makeQuery(id+"F3.opExtrude","CAP_EDGE",EDGE,{"disambiguationData":[OSD([subQ26])],"isStart":true});var subQ30=makeQuery(id+"F1.opExtrude","SWEPT_FACE",FACE,{"disambiguationData":[OSD([subQ18,subQ9])]});var subQ31=makeQuery(id+"F1.opExtrude","SWEPT_FACE",FACE,{"disambiguationData":[OSD([subQ5])]});var subQ32=makeQuery(id+"F1.opExtrude","SWEPT_FACE",FACE,{"disambiguationData":[OSD([subQ10])]});var subQ33=makeQuery(id+"F1.opExtrude","SWEPT_FACE",FACE,{"disambiguationData":[OSD([subQ15])]});var subQ34=makeQuery(id+"F1.opExtrude","SWEPT_FACE",FACE,{"disambiguationData":[OSD([subQ17])]});Q6=makeQuery(id+"F8.opFillet","BLEND_EDGE",EDGE,{"blendedFrom":[makeQuery(id+"F5.boolean.opBoolean","MERGE",EDGE,{"derivedFrom":[makeQuery(id+"F3.boolean.opBoolean","SPLIT",EDGE,{"disambiguationData":[topologyDisambiguationEdgeConnected([subQ27,subQ28]),TD([subQ34])],"derivedFrom":subQ29}),makeQuery(id+"F3.boolean.opBoolean","SPLIT",EDGE,{"disambiguationData":[topologyDisambiguationEdgeConnected([subQ27,subQ28]),TD([subQ32])],"derivedFrom":subQ29}),makeQuery(id+"F3.boolean.opBoolean","SPLIT",EDGE,{"disambiguationData":[topologyDisambiguationEdgeConnected([subQ23,subQ27]),TD([subQ34])],"derivedFrom":subQ29}),makeQuery(id+"F3.boolean.opBoolean","SPLIT",EDGE,{"disambiguationData":[topologyDisambiguationEdgeConnected([subQ23,subQ27]),TD([subQ33])],"derivedFrom":subQ29}),makeQuery(id+"F3.boolean.opBoolean","SPLIT",EDGE,{"disambiguationData":[topologyDisambiguationEdgeConnected([subQ23,subQ27]),TD([subQ32])],"derivedFrom":subQ29}),makeQuery(id+"F3.boolean.opBoolean","SPLIT",EDGE,{"disambiguationData":[topologyDisambiguationEdgeConnected([subQ23,subQ27]),TD([subQ31])],"derivedFrom":subQ29}),makeQuery(id+"F3.boolean.opBoolean","SPLIT",EDGE,{"disambiguationData":[topologyDisambiguationEdgeConnected([subQ27,subQ28]),TD([subQ30])],"derivedFrom":subQ29}),makeQuery(id+"F3.boolean.opBoolean","SPLIT",EDGE,{"disambiguationData":[topologyDisambiguationEdgeConnected([subQ27,subQ28]),TD([subQ25])],"derivedFrom":subQ29})]}),makeQuery(id+"F5.boolean.opBoolean","SPLIT",FACE,{"disambiguationData":[TD([makeQuery(id+"F1.opExtrude","SWEPT_FACE",FACE,{"disambiguationData":[OSD([subQ0])]})])],"derivedFrom":subQ25})],"blendedInto":[makeQuery(id+"F5.boolean.opBoolean","SPLIT",FACE,{"disambiguationData":[TD([makeQuery(id+"F1.opExtrude","SWEPT_FACE",FACE,{"disambiguationData":[OSD([subQ0])]})])],"derivedFrom":subQ25})]});}
            var Q7;
            {var subQ0=sQuery(id+"F0.wireOp",EDGE,"E21.MirrorCS");var subQ1=sQuery(id+"F0.wireOp",EDGE,"E11.MirrorCS");var subQ2=sQuery(id+"F4.wireOp",EDGE,"E27");Q7=makeQuery(id+"F5.boolean.opBoolean","SPLIT",EDGE,{"disambiguationData":[TD([makeQuery(id+"F1.opExtrude","SWEPT_FACE",FACE,{"disambiguationData":[OSD([subQ1,subQ0])]})])],"derivedFrom":makeQuery(id+"F5.opExtrude","CAP_EDGE",EDGE,{"disambiguationData":[OSD([subQ2])],"isStart":true})});}
            var Q8;
            {var subQ1=sQuery(id+"F0.wireOp",EDGE,"E12.MirrorCS");var subQ2=sQuery(id+"F0.wireOp",EDGE,"E21.MirrorCS");var subQ3=sQuery(id+"F0.wireOp",EDGE,"E11.MirrorCS");Q8=makeQuery(id+"F5.boolean.opBoolean","SPLIT",EDGE,{"disambiguationData":[TD([makeQuery(id+"F1.opExtrude","SWEPT_FACE",FACE,{"disambiguationData":[OSD([subQ1])]})])],"derivedFrom":makeQuery(id+"F1.opExtrude","CAP_EDGE",EDGE,{"disambiguationData":[OSD([subQ3,subQ2])],"isStart":true})});}
            var Q9;
            {var subQ1=sQuery(id+"F0.wireOp",EDGE,"E22.MirrorCS");var subQ2=sQuery(id+"F0.wireOp",EDGE,"E21.MirrorCS");var subQ3=sQuery(id+"F0.wireOp",EDGE,"E11.MirrorCS");Q9=makeQuery(id+"F5.boolean.opBoolean","SPLIT",EDGE,{"disambiguationData":[TD([makeQuery(id+"F1.opExtrude","SWEPT_FACE",FACE,{"disambiguationData":[OSD([subQ1])]})])],"derivedFrom":makeQuery(id+"F1.opExtrude","CAP_EDGE",EDGE,{"disambiguationData":[OSD([subQ3,subQ2])],"isStart":true})});}
            var Q10;
            {var subQ1=sQuery(id+"F4.wireOp",EDGE,"E27");var subQ2=sQuery(id+"F0.wireOp",EDGE,"E16.MirrorCS");var subQ3=sQuery(id+"F0.wireOp",EDGE,"E4");var subQ4=makeQuery(id+"F1.opExtrude","SWEPT_FACE",FACE,{"disambiguationData":[OSD([subQ3,subQ2])]});var subQ5=sQuery(id+"F0.wireOp",EDGE,"E24.MirrorCS");var subQ6=sQuery(id+"F0.wireOp",EDGE,"E23.MirrorCS");var subQ7=sQuery(id+"F0.wireOp",EDGE,"E22.MirrorCS");var subQ8=sQuery(id+"F0.wireOp",EDGE,"E21.MirrorCS");var subQ9=sQuery(id+"F0.wireOp",EDGE,"E20.MirrorCS");var subQ10=sQuery(id+"F0.wireOp",EDGE,"E19.MirrorCS");var subQ11=sQuery(id+"F0.wireOp",EDGE,"E18.MirrorCS");var subQ12=sQuery(id+"F0.wireOp",EDGE,"E17.MirrorCS");var subQ13=sQuery(id+"F0.wireOp",EDGE,"E15.MirrorCS");var subQ14=sQuery(id+"F0.wireOp",EDGE,"E14.MirrorCS");var subQ15=sQuery(id+"F0.wireOp",EDGE,"E13.MirrorCS");var subQ16=sQuery(id+"F0.wireOp",EDGE,"E12.MirrorCS");var subQ17=sQuery(id+"F0.wireOp",EDGE,"E11.MirrorCS");var subQ18=sQuery(id+"F0.wireOp",EDGE,"E10.MirrorCS");var subQ19=sQuery(id+"F0.wireOp",EDGE,"E6");var subQ20=sQuery(id+"F0.wireOp",EDGE,"E5");var subQ21=sQuery(id+"F0.wireOp",EDGE,"E3");var subQ22=sQuery(id+"F0.wireOp",EDGE,"E2");var subQ23=sQuery(id+"F0.wireOp",EDGE,"E1");var subQ24=sQuery(id+"F0.wireOp",EDGE,"E0");var subQ25=makeQuery(id+"F1.opExtrude","CAP_FACE",FACE,{"disambiguationData":[OSD([subQ24,subQ23,subQ22,subQ21,subQ3,subQ20,subQ19,subQ18,subQ17,subQ16,subQ15,subQ14,subQ13,subQ2,subQ12,subQ11,subQ10,subQ9,subQ8,subQ7,subQ6,subQ5])],"isStart":false});var subQ26=makeQuery(id+"F1.opExtrude","SWEPT_FACE",FACE,{"disambiguationData":[OSD([subQ17,subQ8])]});var subQ27=sQuery(id+"F2.wireOp",EDGE,"E25");var subQ28=makeQuery(id+"F3.opExtrude","SWEPT_FACE",FACE,{"disambiguationData":[OSD([subQ27])]});var subQ29=makeQuery(id+"F3.opExtrude","CAP_FACE",FACE,{"disambiguationData":[OSD([subQ27,sQuery(id+"F2.wireOp",EDGE,"E26")])],"isStart":true});var subQ30=makeQuery(id+"F3.opExtrude","CAP_EDGE",EDGE,{"disambiguationData":[OSD([subQ27])],"isStart":true});var subQ31=makeQuery(id+"F1.opExtrude","SWEPT_FACE",FACE,{"disambiguationData":[OSD([subQ9])]});var subQ32=makeQuery(id+"F1.opExtrude","SWEPT_FACE",FACE,{"disambiguationData":[OSD([subQ13])]});var subQ33=makeQuery(id+"F1.opExtrude","SWEPT_FACE",FACE,{"disambiguationData":[OSD([subQ18])]});var subQ34=makeQuery(id+"F1.opExtrude","SWEPT_FACE",FACE,{"disambiguationData":[OSD([subQ20])]});Q10=makeQuery(id+"F8.opFillet","BLEND_EDGE",EDGE,{"blendedFrom":[makeQuery(id+"F5.boolean.opBoolean","MERGE",EDGE,{"derivedFrom":[makeQuery(id+"F3.boolean.opBoolean","SPLIT",EDGE,{"disambiguationData":[topologyDisambiguationEdgeConnected([subQ28,subQ29]),TD([subQ34])],"derivedFrom":subQ30}),makeQuery(id+"F3.boolean.opBoolean","SPLIT",EDGE,{"disambiguationData":[topologyDisambiguationEdgeConnected([subQ28,subQ29]),TD([subQ32])],"derivedFrom":subQ30}),makeQuery(id+"F3.boolean.opBoolean","SPLIT",EDGE,{"disambiguationData":[topologyDisambiguationEdgeConnected([subQ25,subQ28]),TD([subQ34])],"derivedFrom":subQ30}),makeQuery(id+"F3.boolean.opBoolean","SPLIT",EDGE,{"disambiguationData":[topologyDisambiguationEdgeConnected([subQ25,subQ28]),TD([subQ33])],"derivedFrom":subQ30}),makeQuery(id+"F3.boolean.opBoolean","SPLIT",EDGE,{"disambiguationData":[topologyDisambiguationEdgeConnected([subQ25,subQ28]),TD([subQ32])],"derivedFrom":subQ30}),makeQuery(id+"F3.boolean.opBoolean","SPLIT",EDGE,{"disambiguationData":[topologyDisambiguationEdgeConnected([subQ25,subQ28]),TD([subQ31])],"derivedFrom":subQ30}),makeQuery(id+"F3.boolean.opBoolean","SPLIT",EDGE,{"disambiguationData":[topologyDisambiguationEdgeConnected([subQ28,subQ29]),TD([subQ4])],"derivedFrom":subQ30}),makeQuery(id+"F3.boolean.opBoolean","SPLIT",EDGE,{"disambiguationData":[topologyDisambiguationEdgeConnected([subQ28,subQ29]),TD([subQ26])],"derivedFrom":subQ30})]}),makeQuery(id+"F5.boolean.opBoolean","SPLIT",FACE,{"disambiguationData":[TD([subQ4])],"derivedFrom":makeQuery(id+"F5.opExtrude","SWEPT_FACE",FACE,{"disambiguationData":[OSD([subQ1])]})})],"blendedInto":[makeQuery(id+"F5.boolean.opBoolean","SPLIT",FACE,{"disambiguationData":[TD([subQ4])],"derivedFrom":makeQuery(id+"F5.opExtrude","SWEPT_FACE",FACE,{"disambiguationData":[OSD([subQ1])]})})]});}
            var Q11;
            {var subQ1=sQuery(id+"F0.wireOp",EDGE,"E3");var subQ2=sQuery(id+"F0.wireOp",EDGE,"E16.MirrorCS");var subQ3=sQuery(id+"F0.wireOp",EDGE,"E4");var subQ4=makeQuery(id+"F1.opExtrude","SWEPT_FACE",FACE,{"disambiguationData":[OSD([subQ3,subQ2])]});var subQ5=makeQuery(id+"F1.opExtrude","CAP_FACE",FACE,{"disambiguationData":[OSD([sQuery(id+"F0.wireOp",EDGE,"E0"),sQuery(id+"F0.wireOp",EDGE,"E1"),sQuery(id+"F0.wireOp",EDGE,"E2"),subQ1,subQ3,sQuery(id+"F0.wireOp",EDGE,"E5"),sQuery(id+"F0.wireOp",EDGE,"E6"),sQuery(id+"F0.wireOp",EDGE,"E10.MirrorCS"),sQuery(id+"F0.wireOp",EDGE,"E11.MirrorCS"),sQuery(id+"F0.wireOp",EDGE,"E12.MirrorCS"),sQuery(id+"F0.wireOp",EDGE,"E13.MirrorCS"),sQuery(id+"F0.wireOp",EDGE,"E14.MirrorCS"),sQuery(id+"F0.wireOp",EDGE,"E15.MirrorCS"),subQ2,sQuery(id+"F0.wireOp",EDGE,"E17.MirrorCS"),sQuery(id+"F0.wireOp",EDGE,"E18.MirrorCS"),sQuery(id+"F0.wireOp",EDGE,"E19.MirrorCS"),sQuery(id+"F0.wireOp",EDGE,"E20.MirrorCS"),sQuery(id+"F0.wireOp",EDGE,"E21.MirrorCS"),sQuery(id+"F0.wireOp",EDGE,"E22.MirrorCS"),sQuery(id+"F0.wireOp",EDGE,"E23.MirrorCS"),sQuery(id+"F0.wireOp",EDGE,"E24.MirrorCS")])],"isStart":false});Q11=makeQuery(id+"F3.boolean.opBoolean","SPLIT",EDGE,{"disambiguationData":[topologyDisambiguationEdgeConnected([subQ5,subQ4]),TD([makeQuery(id+"F1.opExtrude","SWEPT_FACE",FACE,{"disambiguationData":[OSD([subQ1])]})])],"derivedFrom":makeQuery(id+"F1.opExtrude","CAP_EDGE",EDGE,{"disambiguationData":[OSD([subQ3,subQ2])],"isStart":false})});}
            var Q12;
            {var subQ1=sQuery(id+"F0.wireOp",EDGE,"E17.MirrorCS");var subQ2=sQuery(id+"F0.wireOp",EDGE,"E16.MirrorCS");var subQ3=sQuery(id+"F0.wireOp",EDGE,"E4");var subQ4=makeQuery(id+"F1.opExtrude","SWEPT_FACE",FACE,{"disambiguationData":[OSD([subQ3,subQ2])]});var subQ5=makeQuery(id+"F1.opExtrude","CAP_FACE",FACE,{"disambiguationData":[OSD([sQuery(id+"F0.wireOp",EDGE,"E0"),sQuery(id+"F0.wireOp",EDGE,"E1"),sQuery(id+"F0.wireOp",EDGE,"E2"),sQuery(id+"F0.wireOp",EDGE,"E3"),subQ3,sQuery(id+"F0.wireOp",EDGE,"E5"),sQuery(id+"F0.wireOp",EDGE,"E6"),sQuery(id+"F0.wireOp",EDGE,"E10.MirrorCS"),sQuery(id+"F0.wireOp",EDGE,"E11.MirrorCS"),sQuery(id+"F0.wireOp",EDGE,"E12.MirrorCS"),sQuery(id+"F0.wireOp",EDGE,"E13.MirrorCS"),sQuery(id+"F0.wireOp",EDGE,"E14.MirrorCS"),sQuery(id+"F0.wireOp",EDGE,"E15.MirrorCS"),subQ2,subQ1,sQuery(id+"F0.wireOp",EDGE,"E18.MirrorCS"),sQuery(id+"F0.wireOp",EDGE,"E19.MirrorCS"),sQuery(id+"F0.wireOp",EDGE,"E20.MirrorCS"),sQuery(id+"F0.wireOp",EDGE,"E21.MirrorCS"),sQuery(id+"F0.wireOp",EDGE,"E22.MirrorCS"),sQuery(id+"F0.wireOp",EDGE,"E23.MirrorCS"),sQuery(id+"F0.wireOp",EDGE,"E24.MirrorCS")])],"isStart":false});Q12=makeQuery(id+"F3.boolean.opBoolean","SPLIT",EDGE,{"disambiguationData":[topologyDisambiguationEdgeConnected([subQ5,subQ4]),TD([makeQuery(id+"F1.opExtrude","SWEPT_FACE",FACE,{"disambiguationData":[OSD([subQ1])]})])],"derivedFrom":makeQuery(id+"F1.opExtrude","CAP_EDGE",EDGE,{"disambiguationData":[OSD([subQ3,subQ2])],"isStart":false})});}
            var Q13;
            {var subQ0=sQuery(id+"F0.wireOp",EDGE,"E16.MirrorCS");var subQ1=sQuery(id+"F0.wireOp",EDGE,"E4");var subQ2=sQuery(id+"F4.wireOp",EDGE,"E27");Q13=makeQuery(id+"F5.boolean.opBoolean","SPLIT",EDGE,{"disambiguationData":[TD([makeQuery(id+"F1.opExtrude","SWEPT_FACE",FACE,{"disambiguationData":[OSD([subQ1,subQ0])]})])],"derivedFrom":makeQuery(id+"F5.opExtrude","CAP_EDGE",EDGE,{"disambiguationData":[OSD([subQ2])],"isStart":true})});}
            var Q14;
            {var subQ1=sQuery(id+"F0.wireOp",EDGE,"E3");var subQ2=sQuery(id+"F0.wireOp",EDGE,"E16.MirrorCS");var subQ3=sQuery(id+"F0.wireOp",EDGE,"E4");Q14=makeQuery(id+"F5.boolean.opBoolean","SPLIT",EDGE,{"disambiguationData":[TD([makeQuery(id+"F1.opExtrude","SWEPT_FACE",FACE,{"disambiguationData":[OSD([subQ1])]})])],"derivedFrom":makeQuery(id+"F1.opExtrude","CAP_EDGE",EDGE,{"disambiguationData":[OSD([subQ3,subQ2])],"isStart":true})});}
            var Q15;
            {var subQ1=sQuery(id+"F0.wireOp",EDGE,"E16.MirrorCS");var subQ2=sQuery(id+"F0.wireOp",EDGE,"E4");var subQ3=sQuery(id+"F0.wireOp",EDGE,"E17.MirrorCS");Q15=makeQuery(id+"F5.boolean.opBoolean","SPLIT",EDGE,{"disambiguationData":[TD([makeQuery(id+"F1.opExtrude","SWEPT_FACE",FACE,{"disambiguationData":[OSD([subQ3])]})])],"derivedFrom":makeQuery(id+"F1.opExtrude","CAP_EDGE",EDGE,{"disambiguationData":[OSD([subQ2,subQ1])],"isStart":true})});}
            var Q16;
            Q16=makeQuery(id+"F1.opExtrude","CAP_EDGE",EDGE,{"disambiguationData":[OSD([sQuery(id+"F0.wireOp",EDGE,"E6")])],"isStart":true});
            var Q17;
            Q17=makeQuery(id+"F1.opExtrude","CAP_EDGE",EDGE,{"disambiguationData":[OSD([sQuery(id+"F0.wireOp",EDGE,"E6")])],"isStart":false});
            chamfer(context, id + "F9", {"entities" : qUnion([Q0, Q1, Q2, Q3, Q4, Q5, Q6, Q7, Q8, Q9, Q10, Q11, Q12, Q13, Q14, Q15, Q16, Q17]), "width" : 1 * mm, "tangentPropagation" : true});
        }
    });
